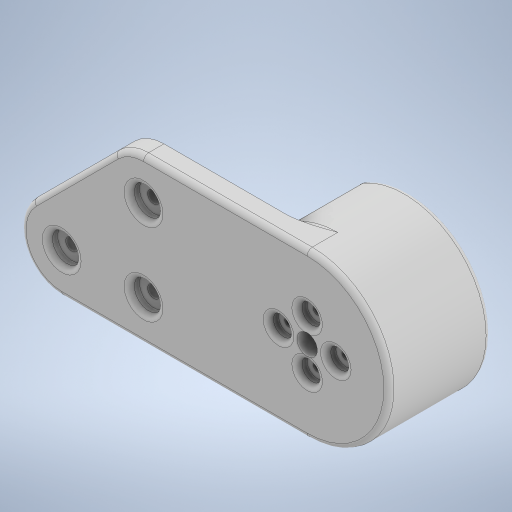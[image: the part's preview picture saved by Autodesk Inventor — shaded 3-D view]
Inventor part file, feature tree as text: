
AUTODESK INVENTOR PART (.ipt)
format: ipt  version: 2024 (Build 280153000, 153)  size: 422,400 bytes
history: native  units: in
note: dims shown in document units (in); Inventor stores cm internally (conversion verified against a paired STEP export)
features: extrude x8, sketch x6, projected_geometry x6, fillet x4
ambient origin geometry x8: Origin, YZ Plane, XZ Plane, XY Plane, X Axis, Y Axis, Z Axis, Center Point
bodies: Solid1 (feature_tree)
feature tree (24):
  extrude  "Extrusion1"  Depth=2.0in
  sketch  "Sketch2"  dims[d2=0.25in d3=0.0in d4=0.15in]
  extrude  "Extrusion2"  Depth=0.25in
  extrude  "Extrusion3"  Depth=1.0in
  sketch  "Sketch3"  dims[d5=0.35in d6=1.0in]
  extrude  "Extrusion4"  Depth=1.0in
  extrude  "Extrusion5"  TaperAngle=0.0deg  [1 undecoded]
  extrude  "Extrusion6"  Depth=0.0625in
  extrude  "Extrusion7"  Depth=0.0625in
  fillet  "Fillet1"  Radius=0.3in
  extrude  "Extrusion8"  Depth=0.0625in
  fillet  "Fillet2"  Radius=0.1in
  fillet  "Fillet3"  Radius=0.25in
  fillet  "Fillet4"  Radius=1.0in
  sketch  "Sketch1"  dims[d0=4.5in d1=2.0in]
  projected_geometry  "Projected Loop1"
  projected_geometry  "Projected Loop2"
  sketch  "Sketch4"  dims[d7=1.0in d8=0.5in]
  projected_geometry  "Projected Loop3"
  sketch  "Sketch5"  dims[d10=0.5in d12=0.0in d13=0.0in]
  projected_geometry  "Projected Loop4"
  projected_geometry  "Projected Loop5"
  sketch  "Sketch6"  dims[d14=0.125in d15=0.0in d16=0.35in d17=0.35in d18=0.3in d19=0.3in d20=0.1in d21=0.25in d22=1.0in d23=0.0in d24=0.0in d25=0.125in d26=0.0in d27=1.5in d28=60.0deg d29=60.0deg d30=1.0in d31=0.0in d32=0.0in d33=0.0in d34=0.0625in d35=0.0in d36=0.0in d37=0.0625in d38=0.125in d39=0.0625in]
  projected_geometry  "Projected Loop6"
note: 1 required parameter value undecoded (feature->parameter linkage not recoverable at this tier; creation-order binding heuristic only, values carry confidence <= 0.55)
